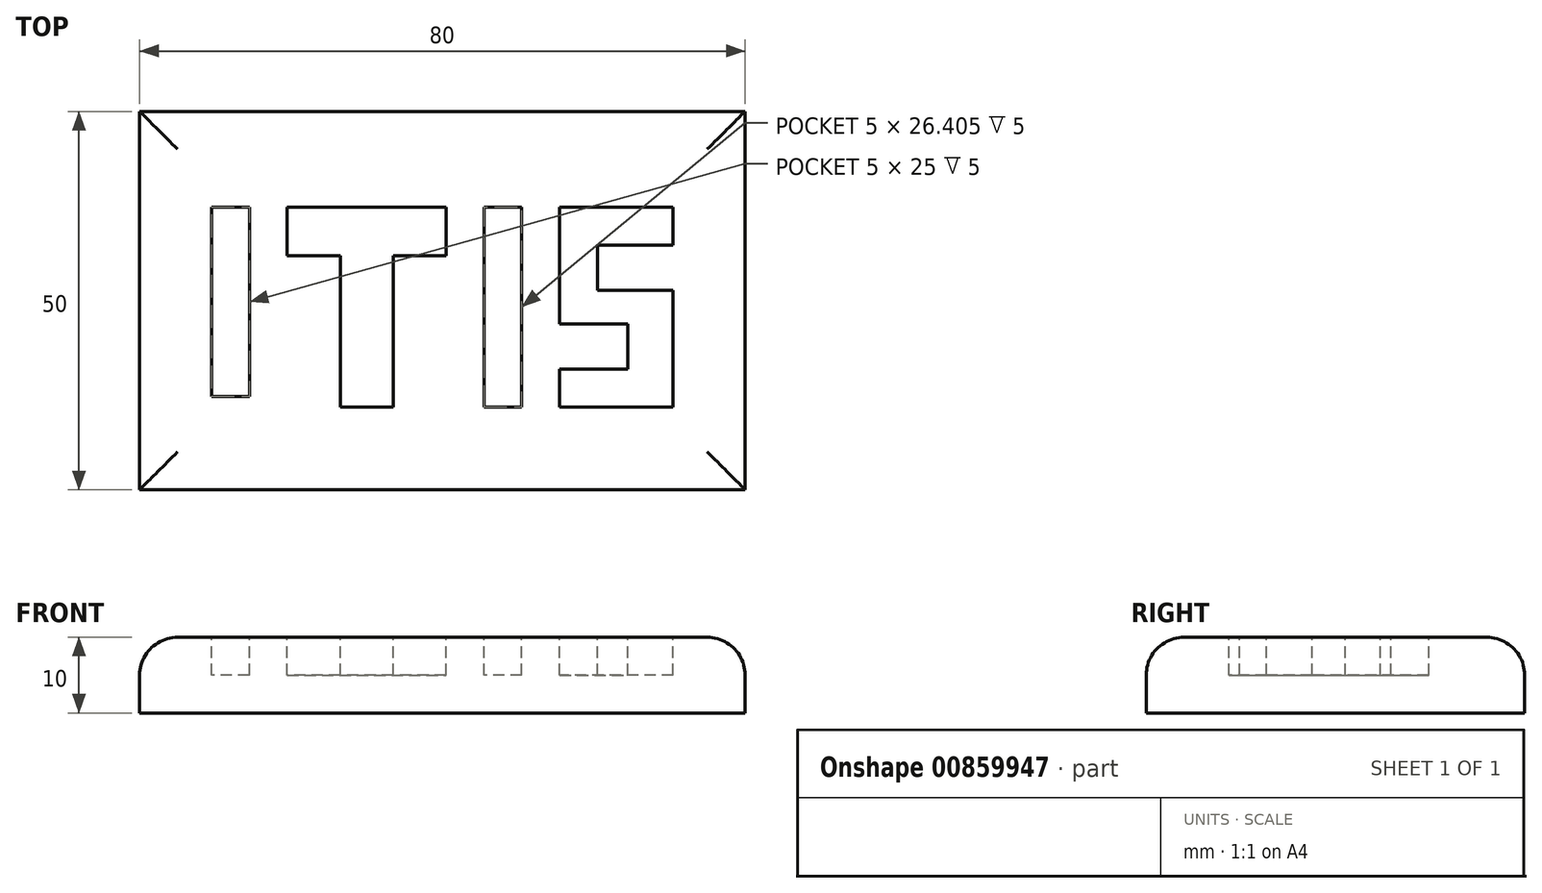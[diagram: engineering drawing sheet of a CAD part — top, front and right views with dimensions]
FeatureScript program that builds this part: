
annotation { "Feature Type Name" : "Feature", "Feature Type Description" : "" }
export const myFeature = defineFeature(function(context is Context, id is Id, definition is map)
    precondition{}
    {
        {
            var Q0;
            Q0=qCreatedBy(makeId("Top.planeOp"),FACE);
            var sketch = newSketch(context, id + "F0", { "sketchPlane" : qUnion([Q0])});
            skLineSegment(sketch, "E0.bottom", {"start": v(0, 0) * mm, "end": v(80, 0) * mm});
            skLineSegment(sketch, "E0.top", {"start": v(0, 50) * mm, "end": v(80, 50) * mm});
            skLineSegment(sketch, "E0.left", {"start": v(0, 0) * mm, "end": v(0, 50) * mm});
            skLineSegment(sketch, "E0.right", {"start": v(80, 0) * mm, "end": v(80, 50) * mm});
            skSolve(sketch);
        }
        {
            var Q0;
            Q0 = qSketchRegion(id + "F0", true);
            extrude(context, id + "F1", {"entities" : qUnion([Q0]), "depth" : 10 * mm, "offsetDistance" : 25 * mm});
        }
        {
            var Q0;
            Q0=makeQuery(id+"F1.opExtrude","CAP_FACE",FACE,{"disambiguationData":[OSD([sQuery(id+"F0.wireOp",EDGE,"E0.bottom"),sQuery(id+"F0.wireOp",EDGE,"E0.top"),sQuery(id+"F0.wireOp",EDGE,"E0.left"),sQuery(id+"F0.wireOp",EDGE,"E0.right")])],"isStart":false});
            var sketch = newSketch(context, id + "F2", { "sketchPlane" : qUnion([Q0])});
            skLineSegment(sketch, "E1", {"start": v(9.5, 12.33) * mm, "end": v(9.5, 37.33) * mm});
            skLineSegment(sketch, "E2", {"start": v(9.5, 37.33) * mm, "end": v(14.5, 37.33) * mm});
            skLineSegment(sketch, "E3", {"start": v(14.5, 37.33) * mm, "end": v(14.5, 12.33) * mm});
            skLineSegment(sketch, "E4", {"start": v(14.5, 12.33) * mm, "end": v(9.5, 12.33) * mm});
            skLineSegment(sketch, "E5", {"start": v(26.5, 10.92) * mm, "end": v(26.5, 30.92) * mm});
            skLineSegment(sketch, "E6", {"start": v(26.5, 30.92) * mm, "end": v(19.5, 30.92) * mm});
            skLineSegment(sketch, "E7", {"start": v(19.5, 30.92) * mm, "end": v(19.5, 37.33) * mm});
            skLineSegment(sketch, "E8", {"start": v(19.5, 37.33) * mm, "end": v(40.5, 37.33) * mm});
            skLineSegment(sketch, "E9", {"start": v(40.5, 37.33) * mm, "end": v(40.5, 30.92) * mm});
            skLineSegment(sketch, "E10", {"start": v(40.5, 30.92) * mm, "end": v(33.5, 30.92) * mm});
            skLineSegment(sketch, "E11", {"start": v(33.5, 30.92) * mm, "end": v(33.5, 10.92) * mm});
            skLineSegment(sketch, "E12", {"start": v(33.5, 10.92) * mm, "end": v(26.5, 10.92) * mm});
            skLineSegment(sketch, "E13", {"start": v(45.5, 10.92) * mm, "end": v(45.5, 37.33) * mm});
            skLineSegment(sketch, "E14", {"start": v(45.5, 37.33) * mm, "end": v(50.5, 37.33) * mm});
            skLineSegment(sketch, "E15", {"start": v(50.5, 37.33) * mm, "end": v(50.5, 10.92) * mm});
            skLineSegment(sketch, "E16", {"start": v(50.5, 10.92) * mm, "end": v(45.5, 10.92) * mm});
            skLineSegment(sketch, "E17", {"start": v(70.5, 37.33) * mm, "end": v(55.5, 37.33) * mm});
            skLineSegment(sketch, "E18", {"start": v(55.5, 37.33) * mm, "end": v(55.5, 21.92) * mm});
            skLineSegment(sketch, "E19", {"start": v(55.5, 21.92) * mm, "end": v(64.5, 21.92) * mm});
            skLineSegment(sketch, "E20", {"start": v(64.5, 21.92) * mm, "end": v(64.5, 15.92) * mm});
            skLineSegment(sketch, "E21", {"start": v(64.5, 15.92) * mm, "end": v(55.5, 15.92) * mm});
            skLineSegment(sketch, "E22", {"start": v(55.5, 15.92) * mm, "end": v(55.5, 10.92) * mm});
            skLineSegment(sketch, "E23", {"start": v(55.5, 10.92) * mm, "end": v(70.5, 10.92) * mm});
            skLineSegment(sketch, "E24", {"start": v(70.5, 10.92) * mm, "end": v(70.5, 26.33) * mm});
            skLineSegment(sketch, "E25", {"start": v(70.5, 26.33) * mm, "end": v(60.5, 26.33) * mm});
            skLineSegment(sketch, "E26", {"start": v(60.5, 26.33) * mm, "end": v(60.5, 32.33) * mm});
            skLineSegment(sketch, "E27", {"start": v(60.5, 32.33) * mm, "end": v(70.5, 32.33) * mm});
            skLineSegment(sketch, "E28", {"start": v(70.5, 32.33) * mm, "end": v(70.5, 37.33) * mm});
            skSolve(sketch);
        }
        {
            var Q0;
            Q0 = qSketchRegion(id + "F2", true);
            extrude(context, id + "F3", {"entities" : qUnion([Q0]), "operationType" : NewBodyOperationType.REMOVE, "oppositeDirection" : true, "depth" : 5 * mm, "offsetDistance" : 25 * mm});
        }
        {
            var Q0;
            Q0=makeQuery(id+"F1.opExtrude","CAP_EDGE",EDGE,{"disambiguationData":[OSD([sQuery(id+"F0.wireOp",EDGE,"E0.left")])],"isStart":false});
            var Q1;
            Q1=makeQuery(id+"F1.opExtrude","CAP_EDGE",EDGE,{"disambiguationData":[OSD([sQuery(id+"F0.wireOp",EDGE,"E0.bottom")])],"isStart":false});
            var Q2;
            Q2=makeQuery(id+"F1.opExtrude","CAP_EDGE",EDGE,{"disambiguationData":[OSD([sQuery(id+"F0.wireOp",EDGE,"E0.right")])],"isStart":false});
            var Q3;
            Q3=makeQuery(id+"F1.opExtrude","CAP_EDGE",EDGE,{"disambiguationData":[OSD([sQuery(id+"F0.wireOp",EDGE,"E0.top")])],"isStart":false});
            fillet(context, id + "F4", {"entities" : qUnion([Q0, Q1, Q2, Q3]), "radius" : 5 * mm, "tangentPropagation" : true, "allowEdgeOverflow" : false});
        }
    });
